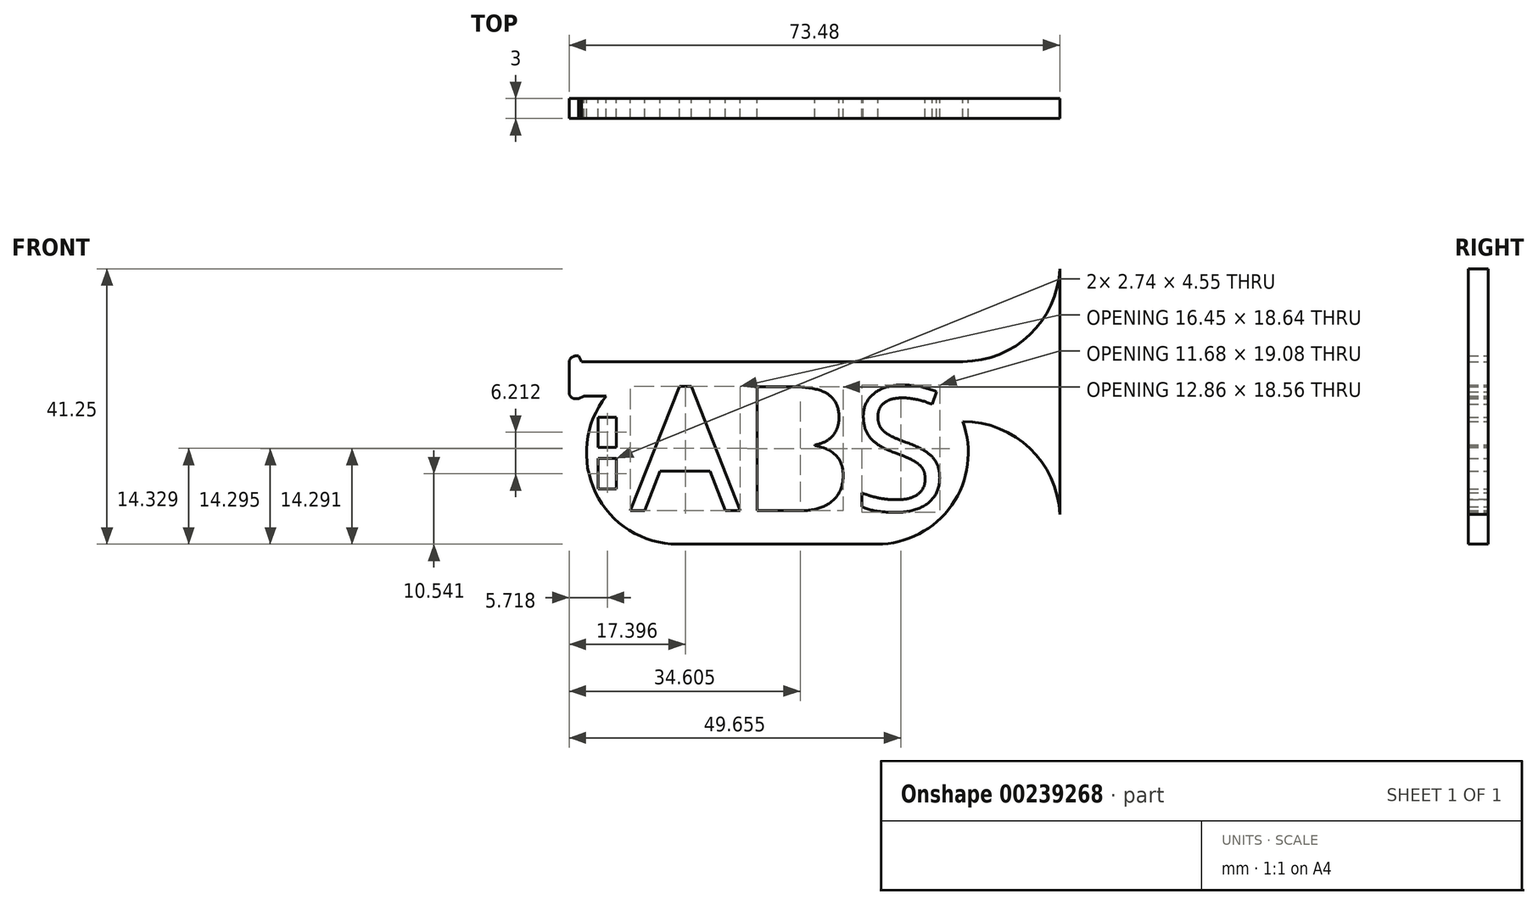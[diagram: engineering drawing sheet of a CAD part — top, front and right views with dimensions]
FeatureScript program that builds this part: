
annotation { "Feature Type Name" : "Feature", "Feature Type Description" : "" }
export const myFeature = defineFeature(function(context is Context, id is Id, definition is map)
    precondition{}
    {
        {
            var Q0;
            Q0=qCreatedBy(makeId("Front.planeOp"),FACE);
            var sketch = newSketch(context, id + "F0", { "sketchPlane" : qUnion([Q0])});
            skArc(sketch, "E0", {"start": v(-10.7, 8.5) * mm, "mid": v(-12.3, -5.95) * mm, "end": v(0, -13.67) * mm});
            skArc(sketch, "E1", {"start": v(29.83, -13.67) * mm, "mid": v(41.04, -7.82) * mm, "end": v(42.66, 4.72) * mm});
            skLineSegment(sketch, "E2", {"start": v(0, 13.67) * mm, "end": v(29.83, 13.67) * mm});
            skLineSegment(sketch, "E3", {"start": v(0, -13.67) * mm, "end": v(29.83, -13.67) * mm});
            skLineSegment(sketch, "E4", {"start": v(0, 13.67) * mm, "end": v(-14.43, 13.67) * mm});
            skLineSegment(sketch, "E5", {"start": v(-14.43, 13.67) * mm, "end": v(-14.83, 14.51) * mm});
            skLineSegment(sketch, "E6", {"start": v(-14.83, 14.51) * mm, "end": v(-15.27, 14.51) * mm});
            skLineSegment(sketch, "E7", {"start": v(-16.27, 13.51) * mm, "end": v(-16.27, 9.1) * mm});
            skLineSegment(sketch, "E8", {"start": v(-15.27, 8.1) * mm, "end": v(-14.83, 8.1) * mm});
            skLineSegment(sketch, "E9", {"start": v(-14.83, 8.1) * mm, "end": v(-13.99, 8.5) * mm});
            skLineSegment(sketch, "E10", {"start": v(-13.99, 8.5) * mm, "end": v(-10.7, 8.5) * mm});
            skPoint(sketch, "E11.visualSharp", {"position": v(-16.27, 14.51) * mm});
            skArc(sketch, "E11.filletArc", {"start": v(-15.27, 14.51) * mm, "mid": v(-15.98, 14.22) * mm, "end": v(-16.27, 13.51) * mm});
            skPoint(sketch, "E12.visualSharp", {"position": v(-16.27, 8.1) * mm});
            skArc(sketch, "E12.filletArc", {"start": v(-16.27, 9.1) * mm, "mid": v(-15.98, 8.4) * mm, "end": v(-15.27, 8.1) * mm});
            skLineSegment(sketch, "E13", {"start": v(29.83, 13.67) * mm, "end": v(42.66, 13.67) * mm});
            skLineSegment(sketch, "E14", {"start": v(42.66, 4.72) * mm, "end": v(42.66, 4.72) * mm});
            skLineSegment(sketch, "E15", {"start": v(42.66, 13.67) * mm, "end": v(42.66, 4.72) * mm, "construction": true});
            skArc(sketch, "E16", {"start": v(42.66, 13.67) * mm, "mid": v(53.19, 18.17) * mm, "end": v(57.21, 28.88) * mm});
            skArc(sketch, "E17", {"start": v(57.21, -9.2) * mm, "mid": v(52.73, 0.68) * mm, "end": v(42.66, 4.72) * mm});
            skLineSegment(sketch, "E18", {"start": v(42.66, 28.23) * mm, "end": v(42.66, -9.84) * mm, "construction": true});
            skLineSegment(sketch, "E19", {"start": v(57.21, 28.88) * mm, "end": v(57.21, -9.2) * mm});
            skLineSegment(sketch, "E20.bottom", {"start": v(-11.92, 5.36) * mm, "end": v(-9.18, 5.36) * mm});
            skLineSegment(sketch, "E20.top", {"start": v(-11.92, -5.4) * mm, "end": v(-9.18, -5.4) * mm});
            skLineSegment(sketch, "E20.left", {"start": v(-11.92, 5.36) * mm, "end": v(-11.92, 0.8) * mm});
            skLineSegment(sketch, "E20.right", {"start": v(-9.18, 5.36) * mm, "end": v(-9.18, 0.8) * mm});
            skPoint(sketch, "E21.endSnap0", {"position": v(-9.18, -0.02) * mm});
            skLineSegment(sketch, "E22.trimOffspring", {"start": v(-11.92, -0.86) * mm, "end": v(-11.92, -5.4) * mm});
            skLineSegment(sketch, "E23.trimOffspring", {"start": v(-9.18, -0.86) * mm, "end": v(-9.18, -5.4) * mm});
            skLineSegment(sketch, "E24", {"start": v(-11.92, 0.8) * mm, "end": v(-9.18, 0.8) * mm});
            skLineSegment(sketch, "E25", {"start": v(-11.92, -0.86) * mm, "end": v(-9.18, -0.86) * mm});
            skPoint(sketch, "E26.orphan", {"position": v(-9.18, 0) * mm});
            skPoint(sketch, "E27.orphan", {"position": v(-11.92, -0.02) * mm});
            skText(sketch, "E28", { "text": "ABS\n", "fontName": "OpenSans-Regular.ttf"});
            const initialGuessF0  = {"E28": [-0.0071, -0.00866, 1, 0, 0.01872]};
            skSetInitialGuess(sketch, initialGuessF0);
            skSolve(sketch);
        }
        {
            var Q0;
            Q0=makeQuery(id+"F0.imprint","IMPRINT",FACE,{"disambiguationData":[TD([[makeQuery(id+"F0.imprint","IMPRINT",EDGE,{"derivedFrom":sQuery(id+"F0.wireOp",EDGE,"E0")}),1.0]])]});
            extrude(context, id + "F1", {"entities" : qUnion([Q0]), "depth" : 3 * mm});
        }
    });
